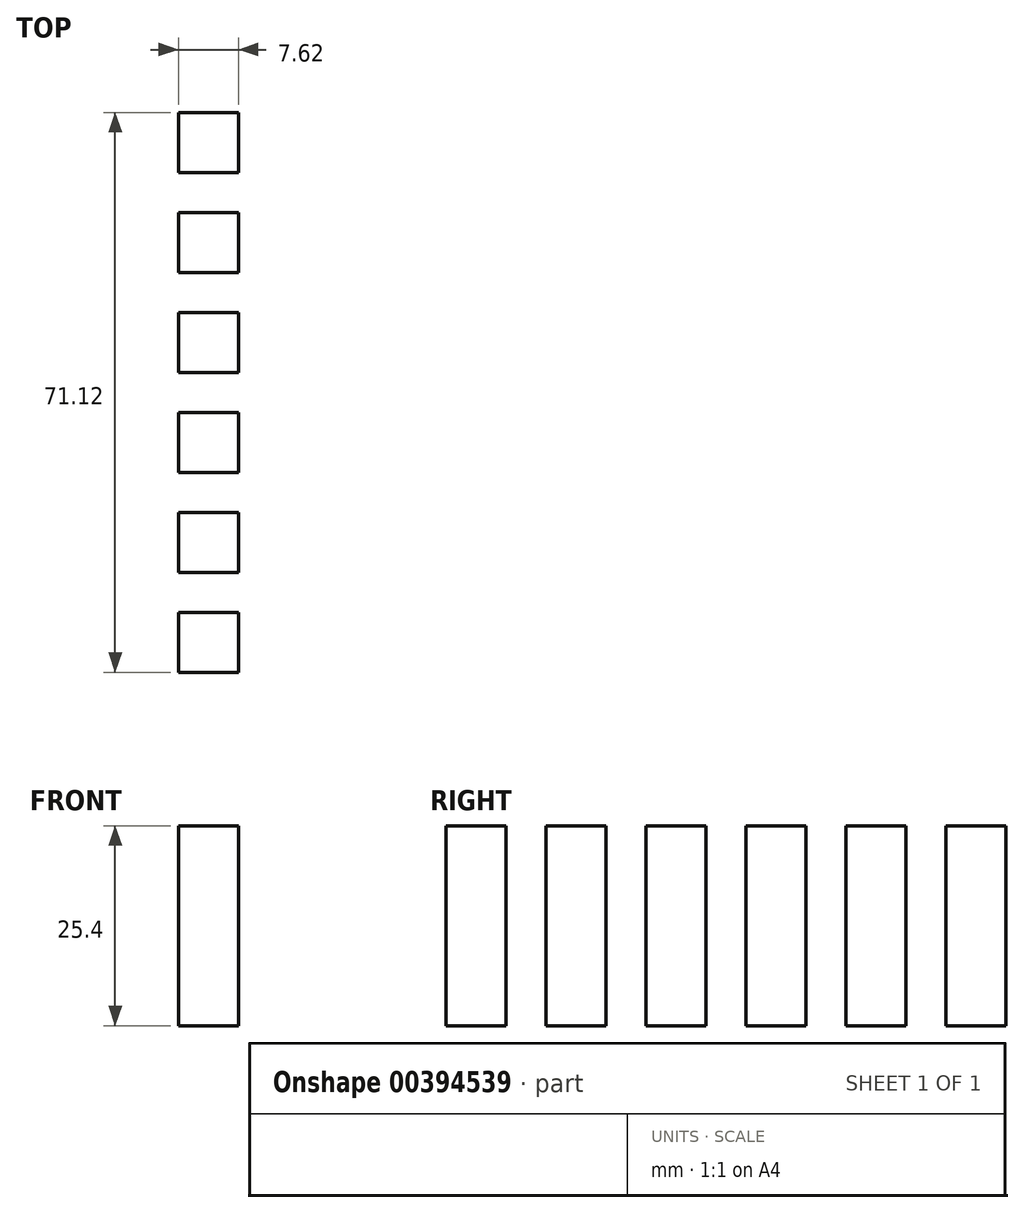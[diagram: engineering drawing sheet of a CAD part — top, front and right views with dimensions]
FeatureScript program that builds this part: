
annotation { "Feature Type Name" : "Feature", "Feature Type Description" : "" }
export const myFeature = defineFeature(function(context is Context, id is Id, definition is map)
    precondition{}
    {
        {
            var Q0;
            Q0=qCreatedBy(makeId("Top.planeOp"),FACE);
            var sketch = newSketch(context, id + "F0", { "sketchPlane" : qUnion([Q0])});
            skLineSegment(sketch, "E0.bottom", {"start": v(34.93, 34.93) * mm, "end": v(-34.92, 34.93) * mm, "construction": true});
            skLineSegment(sketch, "E0.left", {"start": v(34.93, 34.93) * mm, "end": v(34.92, -34.92) * mm, "construction": true});
            skLineSegment(sketch, "E0.right", {"start": v(-34.92, 34.93) * mm, "end": v(-34.93, -34.92) * mm, "construction": true});
            skPoint(sketch, "E0.middle", {"position": v(0, 0) * mm});
            skLineSegment(sketch, "E1", {"start": v(-28.57, 3.18) * mm, "end": v(-28.57, 22.22) * mm});
            skLineSegment(sketch, "E2", {"start": v(-22.22, 28.58) * mm, "end": v(-3.17, 28.58) * mm});
            skLineSegment(sketch, "E3.0", {"start": v(-20.95, 23.5) * mm, "end": v(-3.17, 23.5) * mm});
            skLineSegment(sketch, "E3.1", {"start": v(-23.5, 3.18) * mm, "end": v(-23.5, 20.96) * mm});
            skLineSegment(sketch, "E4.0", {"start": v(-17.14, 18.42) * mm, "end": v(-3.17, 18.42) * mm});
            skLineSegment(sketch, "E4.1", {"start": v(-18.41, 3.18) * mm, "end": v(-18.41, 17.15) * mm});
            skLineSegment(sketch, "E5.0", {"start": v(-13.33, 13.34) * mm, "end": v(-3.17, 13.34) * mm});
            skLineSegment(sketch, "E5.1", {"start": v(-13.33, 3.18) * mm, "end": v(-13.33, 13.34) * mm});
            skPoint(sketch, "E6.visualSharp", {"position": v(-18.41, 18.42) * mm});
            skArc(sketch, "E6.filletArc", {"start": v(-17.14, 18.42) * mm, "mid": v(-18.04, 18.04) * mm, "end": v(-18.41, 17.15) * mm});
            skPoint(sketch, "E7.visualSharp", {"position": v(-23.5, 23.5) * mm});
            skArc(sketch, "E7.filletArc", {"start": v(-20.95, 23.5) * mm, "mid": v(-22.75, 22.75) * mm, "end": v(-23.5, 20.96) * mm});
            skPoint(sketch, "E8.visualSharp", {"position": v(-28.57, 28.58) * mm});
            skArc(sketch, "E8.filletArc", {"start": v(-22.22, 28.57) * mm, "mid": v(-26.72, 26.72) * mm, "end": v(-28.57, 22.22) * mm});
            skLineSegment(sketch, "E9.0", {"start": v(-8.25, 8.25) * mm, "end": v(-3.17, 8.25) * mm});
            skLineSegment(sketch, "E9.1", {"start": v(-8.25, 3.18) * mm, "end": v(-8.25, 8.25) * mm});
            skLineSegment(sketch, "E10", {"start": v(17.46, 17.46) * mm, "end": v(17.46, 34.93) * mm, "construction": true});
            skLineSegment(sketch, "E11", {"start": v(17.46, 34.93) * mm, "end": v(8.73, 26.2) * mm, "construction": true});
            skLineSegment(sketch, "E12", {"start": v(8.73, 26.2) * mm, "end": v(0, 17.46) * mm, "construction": true});
            skLineSegment(sketch, "E13", {"start": v(17.46, 17.46) * mm, "end": v(0, 17.46) * mm, "construction": true});
            skLineSegment(sketch, "E14.bottom", {"start": v(16.35, 33.81) * mm, "end": v(1.11, 33.81) * mm});
            skLineSegment(sketch, "E14.top", {"start": v(16.35, 18.57) * mm, "end": v(1.11, 18.57) * mm});
            skLineSegment(sketch, "E14.left", {"start": v(16.35, 33.81) * mm, "end": v(16.35, 18.57) * mm});
            skLineSegment(sketch, "E14.right", {"start": v(1.11, 33.81) * mm, "end": v(1.11, 18.57) * mm});
            skPoint(sketch, "E14.middle", {"position": v(8.73, 26.2) * mm});
            skLineSegment(sketch, "E15.0", {"start": v(13.81, 31.27) * mm, "end": v(3.65, 31.27) * mm});
            skLineSegment(sketch, "E15.1", {"start": v(13.81, 31.27) * mm, "end": v(13.81, 21.11) * mm});
            skLineSegment(sketch, "E15.2", {"start": v(13.81, 21.11) * mm, "end": v(3.65, 21.11) * mm});
            skLineSegment(sketch, "E15.3", {"start": v(3.65, 31.27) * mm, "end": v(3.65, 21.11) * mm});
            skLineSegment(sketch, "E16.0", {"start": v(11.27, 28.73) * mm, "end": v(6.2, 28.73) * mm});
            skLineSegment(sketch, "E16.1", {"start": v(11.27, 28.73) * mm, "end": v(11.27, 23.65) * mm});
            skLineSegment(sketch, "E16.2", {"start": v(11.27, 23.65) * mm, "end": v(6.2, 23.65) * mm});
            skLineSegment(sketch, "E16.3", {"start": v(6.2, 28.73) * mm, "end": v(6.2, 23.65) * mm});
            skLineSegment(sketch, "E17", {"start": v(0, 34.93) * mm, "end": v(17.46, 17.46) * mm, "construction": true});
            skLineSegment(sketch, "E18.MirrorCS", {"start": v(17.46, 34.93) * mm, "end": v(26.2, 26.2) * mm, "construction": true});
            skLineSegment(sketch, "E19.MirrorCS", {"start": v(34.93, 34.93) * mm, "end": v(17.46, 17.46) * mm, "construction": true});
            skLineSegment(sketch, "E20.MirrorCS", {"start": v(26.2, 26.2) * mm, "end": v(34.93, 17.46) * mm, "construction": true});
            skLineSegment(sketch, "E21.MirrorCS", {"start": v(23.65, 28.73) * mm, "end": v(28.73, 28.73) * mm});
            skLineSegment(sketch, "E22.MirrorCS", {"start": v(21.11, 31.27) * mm, "end": v(31.27, 31.27) * mm});
            skLineSegment(sketch, "E23.MirrorCS", {"start": v(28.73, 28.73) * mm, "end": v(28.73, 23.65) * mm});
            skLineSegment(sketch, "E24.MirrorCS", {"start": v(33.81, 33.81) * mm, "end": v(33.81, 18.57) * mm});
            skLineSegment(sketch, "E25.MirrorCS", {"start": v(18.57, 33.81) * mm, "end": v(33.81, 33.81) * mm});
            skLineSegment(sketch, "E26.MirrorCS", {"start": v(21.11, 31.27) * mm, "end": v(21.11, 21.11) * mm});
            skLineSegment(sketch, "E27.MirrorCS", {"start": v(17.46, 17.46) * mm, "end": v(34.93, 17.46) * mm, "construction": true});
            skLineSegment(sketch, "E28.MirrorCS", {"start": v(23.65, 28.73) * mm, "end": v(23.65, 23.65) * mm});
            skLineSegment(sketch, "E29.MirrorCS", {"start": v(31.27, 31.27) * mm, "end": v(31.27, 21.11) * mm});
            skLineSegment(sketch, "E30.MirrorCS", {"start": v(18.57, 18.57) * mm, "end": v(33.81, 18.57) * mm});
            skLineSegment(sketch, "E31.MirrorCS", {"start": v(23.65, 23.65) * mm, "end": v(28.73, 23.65) * mm});
            skLineSegment(sketch, "E32.MirrorCS", {"start": v(18.57, 33.81) * mm, "end": v(18.57, 18.57) * mm});
            skLineSegment(sketch, "E33.MirrorCS", {"start": v(21.11, 21.11) * mm, "end": v(31.27, 21.11) * mm});
            skPoint(sketch, "E34.MirrorP", {"position": v(26.2, 26.2) * mm});
            skLineSegment(sketch, "E35.MirrorCS", {"start": v(0, 34.93) * mm, "end": v(69.85, 34.93) * mm, "construction": true});
            skLineSegment(sketch, "E36.MirrorCS", {"start": v(21.11, 3.65) * mm, "end": v(31.27, 3.65) * mm});
            skLineSegment(sketch, "E37.MirrorCS", {"start": v(23.65, 6.2) * mm, "end": v(23.65, 11.27) * mm});
            skLineSegment(sketch, "E38.MirrorCS", {"start": v(21.11, 3.65) * mm, "end": v(21.11, 13.81) * mm});
            skLineSegment(sketch, "E39.MirrorCS", {"start": v(33.81, 1.11) * mm, "end": v(33.81, 16.35) * mm});
            skLineSegment(sketch, "E40.MirrorCS", {"start": v(28.73, 6.2) * mm, "end": v(28.73, 11.27) * mm});
            skPoint(sketch, "E41.MirrorP", {"position": v(26.2, 8.73) * mm});
            skLineSegment(sketch, "E42.MirrorCS", {"start": v(23.65, 6.2) * mm, "end": v(28.73, 6.2) * mm});
            skLineSegment(sketch, "E43.MirrorCS", {"start": v(18.57, 16.35) * mm, "end": v(33.81, 16.35) * mm});
            skLineSegment(sketch, "E44.MirrorCS", {"start": v(21.11, 13.81) * mm, "end": v(31.27, 13.81) * mm});
            skLineSegment(sketch, "E45.MirrorCS", {"start": v(23.65, 11.27) * mm, "end": v(28.73, 11.27) * mm});
            skLineSegment(sketch, "E46.MirrorCS", {"start": v(18.57, 1.11) * mm, "end": v(18.57, 16.35) * mm});
            skLineSegment(sketch, "E47.MirrorCS", {"start": v(18.57, 1.11) * mm, "end": v(33.81, 1.11) * mm});
            skLineSegment(sketch, "E48.MirrorCS", {"start": v(31.27, 3.65) * mm, "end": v(31.27, 13.81) * mm});
            skLineSegment(sketch, "E49.MirrorCS", {"start": v(17.46, 17.46) * mm, "end": v(17.46, 0) * mm, "construction": true});
            skLineSegment(sketch, "E50.MirrorCS", {"start": v(34.93, 0) * mm, "end": v(17.46, 17.46) * mm, "construction": true});
            skLineSegment(sketch, "E51.MirrorCS", {"start": v(26.2, 8.73) * mm, "end": v(34.93, 17.46) * mm, "construction": true});
            skLineSegment(sketch, "E52", {"start": v(-31.73, -3.24) * mm, "end": v(-6.33, -3.24) * mm});
            skLineSegment(sketch, "E53.0", {"start": v(-29.85, 3.18) * mm, "end": v(-29.85, 22.23) * mm});
            skArc(sketch, "E53.1", {"start": v(-22.23, 29.84) * mm, "mid": v(-27.61, 27.61) * mm, "end": v(-29.84, 22.23) * mm});
            skLineSegment(sketch, "E53.2", {"start": v(-22.23, 29.85) * mm, "end": v(-3.17, 29.85) * mm});
            skLineSegment(sketch, "E54.0", {"start": v(-24.77, 3.18) * mm, "end": v(-24.77, 20.96) * mm});
            skArc(sketch, "E54.1", {"start": v(-20.96, 24.77) * mm, "mid": v(-23.65, 23.65) * mm, "end": v(-24.76, 20.96) * mm});
            skLineSegment(sketch, "E54.2", {"start": v(-20.96, 24.77) * mm, "end": v(-3.17, 24.77) * mm});
            skLineSegment(sketch, "E55.0", {"start": v(-17.15, 19.69) * mm, "end": v(-3.17, 19.69) * mm});
            skArc(sketch, "E55.1", {"start": v(-17.15, 19.69) * mm, "mid": v(-18.94, 18.94) * mm, "end": v(-19.68, 17.15) * mm});
            skLineSegment(sketch, "E55.2", {"start": v(-19.69, 3.18) * mm, "end": v(-19.69, 17.15) * mm});
            skLineSegment(sketch, "E56.0", {"start": v(-14.6, 14.6) * mm, "end": v(-3.17, 14.6) * mm});
            skLineSegment(sketch, "E56.1", {"start": v(-14.6, 3.18) * mm, "end": v(-14.6, 14.6) * mm});
            skLineSegment(sketch, "E57.0", {"start": v(-9.53, 9.53) * mm, "end": v(-3.17, 9.53) * mm});
            skLineSegment(sketch, "E57.1", {"start": v(-9.53, 3.18) * mm, "end": v(-9.53, 9.53) * mm});
            skLineSegment(sketch, "E58", {"start": v(-3.17, 29.85) * mm, "end": v(-3.17, 28.58) * mm});
            skLineSegment(sketch, "E59", {"start": v(-3.17, 24.77) * mm, "end": v(-3.17, 23.5) * mm});
            skLineSegment(sketch, "E60", {"start": v(-3.17, 19.69) * mm, "end": v(-3.17, 18.42) * mm});
            skLineSegment(sketch, "E61", {"start": v(-3.17, 13.34) * mm, "end": v(-3.17, 14.6) * mm});
            skLineSegment(sketch, "E62", {"start": v(-3.17, 9.53) * mm, "end": v(-3.17, 8.25) * mm});
            skLineSegment(sketch, "E63", {"start": v(-8.25, 3.18) * mm, "end": v(-9.53, 3.18) * mm});
            skLineSegment(sketch, "E64", {"start": v(-13.33, 3.18) * mm, "end": v(-14.6, 3.18) * mm});
            skLineSegment(sketch, "E65", {"start": v(-18.41, 3.18) * mm, "end": v(-19.69, 3.18) * mm});
            skLineSegment(sketch, "E66", {"start": v(-29.85, 3.18) * mm, "end": v(-28.57, 3.18) * mm});
            skLineSegment(sketch, "E67", {"start": v(-24.77, 3.18) * mm, "end": v(-23.5, 3.18) * mm});
            skLineSegment(sketch, "E68", {"start": v(-31.73, -3.24) * mm, "end": v(-31.73, -3.24) * mm});
            skLineSegment(sketch, "E69", {"start": v(-6.33, -3.24) * mm, "end": v(-6.33, -3.24) * mm});
            skLineSegment(sketch, "E70", {"start": v(-34.93, -34.92) * mm, "end": v(34.92, -34.92) * mm, "construction": true});
            skLineSegment(sketch, "E71.0.1.0", {"start": v(-31.73, -8.32) * mm, "end": v(-6.33, -8.32) * mm});
            skLineSegment(sketch, "E71.0.1.1", {"start": v(-31.73, -8.32) * mm, "end": v(-6.33, -8.32) * mm});
            skLineSegment(sketch, "E71.0.1.2", {"start": v(-31.73, -8.32) * mm, "end": v(-31.73, -8.32) * mm});
            skLineSegment(sketch, "E71.0.1.3", {"start": v(-6.33, -8.32) * mm, "end": v(-6.33, -8.32) * mm});
            skLineSegment(sketch, "E71.0.2.0", {"start": v(-31.73, -13.4) * mm, "end": v(-6.33, -13.4) * mm});
            skLineSegment(sketch, "E71.0.2.1", {"start": v(-31.73, -13.4) * mm, "end": v(-6.33, -13.4) * mm});
            skLineSegment(sketch, "E71.0.2.2", {"start": v(-31.73, -13.4) * mm, "end": v(-31.73, -13.4) * mm});
            skLineSegment(sketch, "E71.0.2.3", {"start": v(-6.33, -13.4) * mm, "end": v(-6.33, -13.4) * mm});
            skLineSegment(sketch, "E71.0.3.0", {"start": v(-31.73, -18.48) * mm, "end": v(-6.33, -18.48) * mm});
            skLineSegment(sketch, "E71.0.3.1", {"start": v(-31.73, -18.48) * mm, "end": v(-6.33, -18.48) * mm});
            skLineSegment(sketch, "E71.0.3.2", {"start": v(-31.73, -18.48) * mm, "end": v(-31.73, -18.48) * mm});
            skLineSegment(sketch, "E71.0.3.3", {"start": v(-6.33, -18.48) * mm, "end": v(-6.33, -18.48) * mm});
            skLineSegment(sketch, "E71.0.4.0", {"start": v(-31.73, -23.56) * mm, "end": v(-6.33, -23.56) * mm});
            skLineSegment(sketch, "E71.0.4.1", {"start": v(-31.73, -23.56) * mm, "end": v(-6.33, -23.56) * mm});
            skLineSegment(sketch, "E71.0.4.2", {"start": v(-31.73, -23.56) * mm, "end": v(-31.73, -23.56) * mm});
            skLineSegment(sketch, "E71.0.4.3", {"start": v(-6.33, -23.56) * mm, "end": v(-6.33, -23.56) * mm});
            skLineSegment(sketch, "E71.0.5.0", {"start": v(-31.73, -28.64) * mm, "end": v(-6.33, -28.64) * mm});
            skLineSegment(sketch, "E71.0.5.1", {"start": v(-31.73, -28.64) * mm, "end": v(-6.33, -28.64) * mm});
            skLineSegment(sketch, "E71.0.5.2", {"start": v(-31.73, -28.64) * mm, "end": v(-31.73, -28.64) * mm});
            skLineSegment(sketch, "E71.0.5.3", {"start": v(-6.33, -28.64) * mm, "end": v(-6.33, -28.64) * mm});
            skLineSegment(sketch, "E71.direction1", {"start": v(-31.73, -3.24) * mm, "end": v(-6.33, -3.24) * mm, "construction": true});
            skLineSegment(sketch, "E71.direction2", {"start": v(-31.73, -3.24) * mm, "end": v(-31.73, -8.32) * mm, "construction": true});
            skLineSegment(sketch, "E72.0", {"start": v(33.82, 33.82) * mm, "end": v(33.82, 18.57) * mm});
            skLineSegment(sketch, "E72.1", {"start": v(18.57, 33.82) * mm, "end": v(33.82, 33.82) * mm});
            skLineSegment(sketch, "E72.2", {"start": v(18.57, 33.82) * mm, "end": v(18.57, 18.57) * mm});
            skLineSegment(sketch, "E72.3", {"start": v(18.57, 18.57) * mm, "end": v(33.82, 18.57) * mm});
            skLineSegment(sketch, "E73.MirrorCS", {"start": v(31.27, 21.11) * mm, "end": v(21.11, 21.11) * mm});
            skLineSegment(sketch, "E74.MirrorCS", {"start": v(21.11, 21.11) * mm, "end": v(21.11, 31.27) * mm});
            skLineSegment(sketch, "E75.MirrorCS", {"start": v(31.27, 31.27) * mm, "end": v(21.11, 31.27) * mm});
            skLineSegment(sketch, "E76.MirrorCS", {"start": v(31.27, 21.11) * mm, "end": v(31.27, 31.27) * mm});
            skLineSegment(sketch, "E77.0", {"start": v(31.28, 31.28) * mm, "end": v(21.11, 31.28) * mm});
            skLineSegment(sketch, "E77.1", {"start": v(31.28, 31.28) * mm, "end": v(31.28, 21.11) * mm});
            skLineSegment(sketch, "E77.2", {"start": v(21.11, 21.11) * mm, "end": v(31.28, 21.11) * mm});
            skLineSegment(sketch, "E77.3", {"start": v(21.11, 31.28) * mm, "end": v(21.11, 21.11) * mm});
            skLineSegment(sketch, "E78.0", {"start": v(23.65, 28.74) * mm, "end": v(28.74, 28.74) * mm});
            skLineSegment(sketch, "E78.1", {"start": v(23.65, 28.74) * mm, "end": v(23.65, 23.65) * mm});
            skLineSegment(sketch, "E78.2", {"start": v(23.65, 23.65) * mm, "end": v(28.74, 23.65) * mm});
            skLineSegment(sketch, "E78.3", {"start": v(28.74, 28.74) * mm, "end": v(28.74, 23.65) * mm});
            skLineSegment(sketch, "E79.0", {"start": v(16.35, 33.82) * mm, "end": v(1.1, 33.82) * mm});
            skLineSegment(sketch, "E79.1", {"start": v(16.35, 33.82) * mm, "end": v(16.35, 18.57) * mm});
            skLineSegment(sketch, "E79.2", {"start": v(16.35, 18.57) * mm, "end": v(1.1, 18.57) * mm});
            skLineSegment(sketch, "E79.3", {"start": v(1.1, 33.82) * mm, "end": v(1.1, 18.57) * mm});
            skLineSegment(sketch, "E80.0", {"start": v(13.81, 31.28) * mm, "end": v(3.65, 31.28) * mm});
            skLineSegment(sketch, "E80.1", {"start": v(13.81, 31.28) * mm, "end": v(13.81, 21.11) * mm});
            skLineSegment(sketch, "E80.3", {"start": v(3.65, 31.28) * mm, "end": v(3.65, 21.11) * mm});
            skLineSegment(sketch, "E81.0", {"start": v(11.27, 28.74) * mm, "end": v(6.19, 28.74) * mm});
            skLineSegment(sketch, "E81.1", {"start": v(11.27, 28.74) * mm, "end": v(11.27, 23.65) * mm});
            skLineSegment(sketch, "E81.2", {"start": v(11.27, 23.65) * mm, "end": v(6.19, 23.65) * mm});
            skLineSegment(sketch, "E81.3", {"start": v(6.19, 28.74) * mm, "end": v(6.19, 23.65) * mm});
            skLineSegment(sketch, "E82.0", {"start": v(18.57, 1.1) * mm, "end": v(18.57, 16.35) * mm});
            skLineSegment(sketch, "E82.1", {"start": v(18.57, 1.1) * mm, "end": v(33.82, 1.1) * mm});
            skLineSegment(sketch, "E82.2", {"start": v(33.82, 1.1) * mm, "end": v(33.82, 16.35) * mm});
            skLineSegment(sketch, "E82.3", {"start": v(18.57, 16.35) * mm, "end": v(33.82, 16.35) * mm});
            skLineSegment(sketch, "E83.1", {"start": v(21.11, 3.65) * mm, "end": v(31.28, 3.65) * mm});
            skLineSegment(sketch, "E83.2", {"start": v(31.28, 3.65) * mm, "end": v(31.28, 13.81) * mm});
            skLineSegment(sketch, "E83.3", {"start": v(21.11, 13.81) * mm, "end": v(31.28, 13.81) * mm});
            skLineSegment(sketch, "E84.0", {"start": v(28.74, 6.19) * mm, "end": v(28.74, 11.27) * mm});
            skLineSegment(sketch, "E84.1", {"start": v(23.65, 6.19) * mm, "end": v(28.74, 6.19) * mm});
            skLineSegment(sketch, "E84.2", {"start": v(23.65, 6.19) * mm, "end": v(23.65, 11.27) * mm});
            skLineSegment(sketch, "E84.3", {"start": v(23.65, 11.27) * mm, "end": v(28.74, 11.27) * mm});
            skSolve(sketch);
        }
        {
            var Q0;
            Q0=qCreatedBy(makeId("Top.planeOp"),FACE);
            var sketch = newSketch(context, id + "F1", { "sketchPlane" : qUnion([Q0])});
            skLineSegment(sketch, "E85.bottom", {"start": v(22.23, 22.22) * mm, "end": v(-22.23, 22.22) * mm, "construction": true});
            skLineSegment(sketch, "E85.top", {"start": v(22.23, -22.23) * mm, "end": v(-22.23, -22.23) * mm, "construction": true});
            skLineSegment(sketch, "E85.left", {"start": v(22.23, 22.22) * mm, "end": v(22.23, -22.23) * mm, "construction": true});
            skLineSegment(sketch, "E85.right", {"start": v(-22.23, 22.22) * mm, "end": v(-22.23, -22.23) * mm, "construction": true});
            skPoint(sketch, "E85.middle", {"position": v(0, 0) * mm});
            skLineSegment(sketch, "E86", {"start": v(0, 22.23) * mm, "end": v(0, -22.23) * mm, "construction": true});
            skLineSegment(sketch, "E87", {"start": v(0, -22.22) * mm, "end": v(-22.23, 0) * mm, "construction": true});
            skLineSegment(sketch, "E88", {"start": v(-22.23, 0) * mm, "end": v(0, 22.23) * mm, "construction": true});
            skLineSegment(sketch, "E89", {"start": v(0, 22.23) * mm, "end": v(22.23, 0) * mm, "construction": true});
            skLineSegment(sketch, "E90", {"start": v(22.22, 0) * mm, "end": v(0, -22.22) * mm, "construction": true});
            skLineSegment(sketch, "E91", {"start": v(-22.23, 0) * mm, "end": v(22.22, 0) * mm, "construction": true});
            skLineSegment(sketch, "E92.bottom", {"start": v(-4.76, 17.46) * mm, "end": v(-17.46, 17.46) * mm});
            skLineSegment(sketch, "E92.top", {"start": v(-4.76, 4.76) * mm, "end": v(-17.46, 4.76) * mm});
            skLineSegment(sketch, "E92.left", {"start": v(-4.76, 17.46) * mm, "end": v(-4.76, 4.76) * mm});
            skLineSegment(sketch, "E92.right", {"start": v(-17.46, 17.46) * mm, "end": v(-17.46, 4.76) * mm});
            skPoint(sketch, "E92.middle", {"position": v(-11.11, 11.11) * mm});
            skLineSegment(sketch, "E93.MirrorCS", {"start": v(4.76, 17.46) * mm, "end": v(17.46, 17.46) * mm});
            skPoint(sketch, "E94.MirrorP", {"position": v(11.11, 11.11) * mm});
            skLineSegment(sketch, "E95.MirrorCS", {"start": v(4.76, 4.76) * mm, "end": v(17.46, 4.76) * mm});
            skLineSegment(sketch, "E96.MirrorCS", {"start": v(17.46, 17.46) * mm, "end": v(17.46, 4.76) * mm});
            skLineSegment(sketch, "E97.MirrorCS", {"start": v(4.76, 17.46) * mm, "end": v(4.76, 4.76) * mm});
            skLineSegment(sketch, "E98.MirrorCS", {"start": v(17.46, -17.46) * mm, "end": v(17.46, -4.76) * mm});
            skLineSegment(sketch, "E99.MirrorCS", {"start": v(-17.46, -17.46) * mm, "end": v(-17.46, -4.76) * mm});
            skPoint(sketch, "E100.MirrorP", {"position": v(-11.11, -11.11) * mm});
            skLineSegment(sketch, "E101.MirrorCS", {"start": v(-4.76, -17.46) * mm, "end": v(-4.76, -4.76) * mm});
            skLineSegment(sketch, "E102.MirrorCS", {"start": v(4.76, -4.76) * mm, "end": v(17.46, -4.76) * mm});
            skLineSegment(sketch, "E103.MirrorCS", {"start": v(4.76, -17.46) * mm, "end": v(17.46, -17.46) * mm});
            skLineSegment(sketch, "E104.MirrorCS", {"start": v(-4.76, -17.46) * mm, "end": v(-17.46, -17.46) * mm});
            skLineSegment(sketch, "E105.MirrorCS", {"start": v(-4.76, -4.76) * mm, "end": v(-17.46, -4.76) * mm});
            skPoint(sketch, "E106.MirrorP", {"position": v(11.11, -11.11) * mm});
            skLineSegment(sketch, "E107.MirrorCS", {"start": v(4.76, -17.46) * mm, "end": v(4.76, -4.76) * mm});
            skSolve(sketch);
        }
        {
            var Q0;
            Q0=qCreatedBy(makeId("Top.planeOp"),FACE);
            var sketch = newSketch(context, id + "F2", { "sketchPlane" : qUnion([Q0])});
            skLineSegment(sketch, "E108", {"start": v(0, 40.5) * mm, "end": v(0, -35.7) * mm, "construction": true});
            skLineSegment(sketch, "E109.bottom", {"start": v(0, 37.97) * mm, "end": v(7.62, 37.97) * mm});
            skLineSegment(sketch, "E109.top", {"start": v(0, 30.35) * mm, "end": v(7.62, 30.35) * mm});
            skLineSegment(sketch, "E109.left", {"start": v(0, 37.97) * mm, "end": v(0, 30.35) * mm});
            skLineSegment(sketch, "E109.right", {"start": v(7.62, 37.97) * mm, "end": v(7.62, 30.35) * mm});
            skLineSegment(sketch, "E110.0.1.0", {"start": v(0, 25.27) * mm, "end": v(0, 17.65) * mm});
            skLineSegment(sketch, "E110.0.1.1", {"start": v(0, 25.27) * mm, "end": v(7.62, 25.27) * mm});
            skLineSegment(sketch, "E110.0.1.2", {"start": v(0, 17.65) * mm, "end": v(7.62, 17.65) * mm});
            skLineSegment(sketch, "E110.0.1.3", {"start": v(7.62, 25.27) * mm, "end": v(7.62, 17.65) * mm});
            skLineSegment(sketch, "E110.0.2.0", {"start": v(0, 12.57) * mm, "end": v(0, 4.95) * mm});
            skLineSegment(sketch, "E110.0.2.1", {"start": v(0, 12.57) * mm, "end": v(7.62, 12.57) * mm});
            skLineSegment(sketch, "E110.0.2.2", {"start": v(0, 4.95) * mm, "end": v(7.62, 4.95) * mm});
            skLineSegment(sketch, "E110.0.2.3", {"start": v(7.62, 12.57) * mm, "end": v(7.62, 4.95) * mm});
            skLineSegment(sketch, "E110.0.3.0", {"start": v(0, -0.13) * mm, "end": v(0, -7.75) * mm});
            skLineSegment(sketch, "E110.0.3.1", {"start": v(0, -0.13) * mm, "end": v(7.62, -0.13) * mm});
            skLineSegment(sketch, "E110.0.3.2", {"start": v(0, -7.75) * mm, "end": v(7.62, -7.75) * mm});
            skLineSegment(sketch, "E110.0.3.3", {"start": v(7.62, -0.13) * mm, "end": v(7.62, -7.75) * mm});
            skLineSegment(sketch, "E110.0.4.0", {"start": v(0, -12.83) * mm, "end": v(0, -20.45) * mm});
            skLineSegment(sketch, "E110.0.4.1", {"start": v(0, -12.83) * mm, "end": v(7.62, -12.83) * mm});
            skLineSegment(sketch, "E110.0.4.2", {"start": v(0, -20.45) * mm, "end": v(7.62, -20.45) * mm});
            skLineSegment(sketch, "E110.0.4.3", {"start": v(7.62, -12.83) * mm, "end": v(7.62, -20.45) * mm});
            skLineSegment(sketch, "E110.0.5.0", {"start": v(0, -25.53) * mm, "end": v(0, -33.15) * mm});
            skLineSegment(sketch, "E110.0.5.1", {"start": v(0, -25.53) * mm, "end": v(7.62, -25.53) * mm});
            skLineSegment(sketch, "E110.0.5.2", {"start": v(0, -33.15) * mm, "end": v(7.62, -33.15) * mm});
            skLineSegment(sketch, "E110.0.5.3", {"start": v(7.62, -25.53) * mm, "end": v(7.62, -33.15) * mm});
            skLineSegment(sketch, "E110.direction2", {"start": v(0, 30.35) * mm, "end": v(0, 17.65) * mm, "construction": true});
            skSolve(sketch);
        }
        {
            var Q0;
            Q0 = qSketchRegion(id + "F2", true);
            extrude(context, id + "F3", {"entities" : qUnion([Q0]), "depth" : 25.4 * mm});
        }
    });
